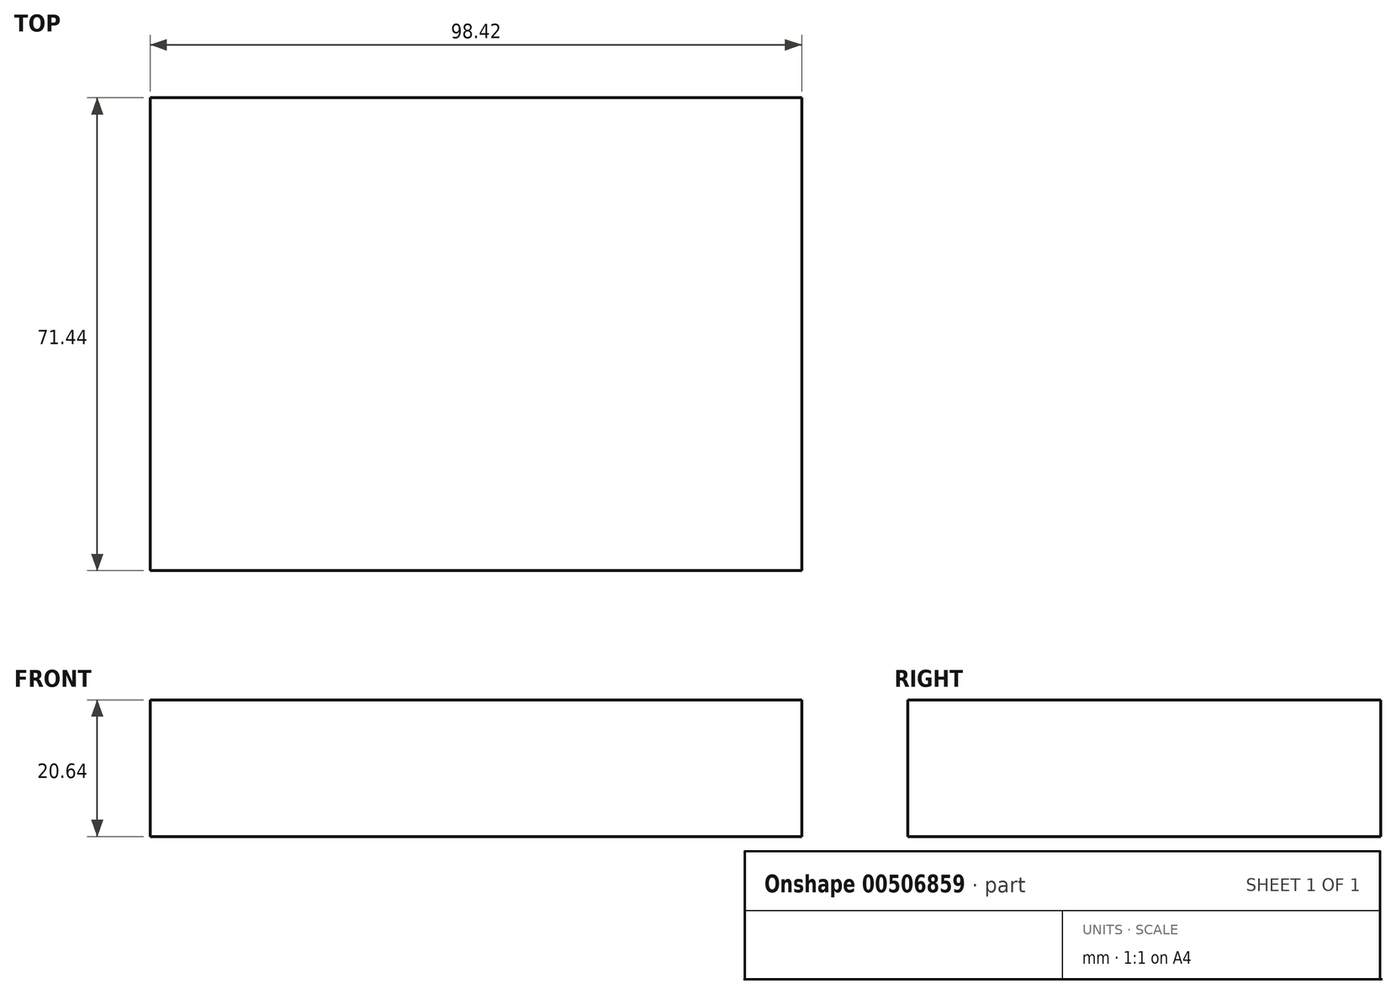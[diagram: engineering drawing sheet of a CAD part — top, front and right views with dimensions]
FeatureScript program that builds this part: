
annotation { "Feature Type Name" : "Feature", "Feature Type Description" : "" }
export const myFeature = defineFeature(function(context is Context, id is Id, definition is map)
    precondition{}
    {
        {
            var Q0;
            Q0=qCreatedBy(makeId("Top.planeOp"),FACE);
            var sketch = newSketch(context, id + "F0", { "sketchPlane" : qUnion([Q0])});
            skLineSegment(sketch, "E0.bottom", {"start": v(-166.01, -72.6) * mm, "end": v(-67.59, -72.6) * mm});
            skLineSegment(sketch, "E0.top", {"start": v(-166.01, -144.03) * mm, "end": v(-67.59, -144.03) * mm});
            skLineSegment(sketch, "E0.left", {"start": v(-166.01, -72.6) * mm, "end": v(-166.01, -144.03) * mm});
            skLineSegment(sketch, "E0.right", {"start": v(-67.59, -72.6) * mm, "end": v(-67.59, -144.03) * mm});
            skSolve(sketch);
        }
        {
            var Q0;
            Q0=makeQuery(id+"F0.imprint","IMPRINT",FACE,{"disambiguationData":[TD([[makeQuery(id+"F0.imprint","IMPRINT",EDGE,{"derivedFrom":sQuery(id+"F0.wireOp",EDGE,"E0.bottom")}),-1.0]])]});
            extrude(context, id + "F1", {"entities" : qUnion([Q0]), "depth" : 20.64 * mm, "offsetDistance" : 25.4 * mm});
        }
    });
